# Revit family: 706630001_Papelera Metálica
name_source: partatom
category: Generic Models
units: mm (PartAtom-declared; Revit-internal decimal feet)

## family parameters
Always vertical = Yes
Can host rebar = No
Cut with Voids When Loaded = No
Host = Wall
OmniClass Number = 23.21.43.11.13
OmniClass Title = Waste Paper Baskets
Part Type = Normal
Room Calculation Point = No
Round Connector Dimension = Use Diameter
Shared = No

## types (1)
- Ref. 706630001 Papelera metálica
    Alto = 400 mm
    Ancho = 310 mm
    Capacidad de carga = 45 kg. - 99,2 lbs.
    Capacidad de volumen = 12 lts. - 3,2 gl.
    Creado por = IDD
    Description = Tamaño ajustado para adecuar en diferentes baños
· Sistema de fijación extrema, ideal para instituciones de alto tráfico
· Fabricación en acero inoxidable ofreciendo mayor calidad y servicio
    Dimensiones Empacado (H x L x W) = 425 x 360 x 185 mm.
16,7 x 14,2 x 7,3 pulg.
    Dimensiones Generales (H x L x W) = 400 x 310 x 130 mm.
15,7 x 12,2 x 5,1 pulg.
    Fecha de creación = 22/07/2020
    Garantía = 1 año
    Garantía Acabados = 3 años
    Manufacturer = Corona
    Material = Corona_Acero inoxidable
    Peso Bruto aprox = 2,8 kg. - 5,6 lbs.
    Peso Neto aprox = 2,6 kg. - 5,2 lbs.
    Profundidad = 130 mm
    URL = https://corona.co

## geometry (parser evidence)
native form markers: Blend x4, Extrusion x1, Sweep x6
no freeform markers — native parametric forms only
